# Revit family: P300300-031
name_source: partatom
category: Lighting Fixtures
revit_build: Autodesk Revit 2014 (Build: 20130308_1515(x64)
units: mm (PartAtom-declared; Revit-internal decimal feet)

## types (1)
- P300300-031
    Apparent Load = 100 VA
    Assembly Code = D5020200
    Connector Description = Lighting Connector
    Default Elevation = 48 "
    Description = Clarion Collection Two-Light Matte Black and Clear Glass Modern Style Bath Vanity Wall Light
    Features = Application: Embrace minimalist simplicity with the Clarion Collection 2-Light Matte Black Clear Glass Modern Bath Vanity Light ideal for any entryway, hallway, foyer, bedroom, sitting room, or bathroom.
Style: Perfect for contemporary, modern, and transitional style settings.
Finish: The square backplate and rounded light base are coated in a beautiful matte black finish for a modern aesthetic.
Materials: Constructed from steel to ensure a long product lifespan. Mount the light fixture vertically or horizontally.
Glass: Light sources glow from inside cylindrical shades for a crisp, clean look.
Bulbs: For ideal illumination, use 2 medium base T-lamp bulbs that are sold separately (60w max - LED/CFL/incandescent). Compatible with dimmable bulbs.
Dimensions: Measures 20-3/8-inch width by 5-inch height by 4-inch extends.
Certifications: cULus damp location listed.
Pairs With: Pairs with Equinox, Cahill, and Bonita collections.
Warranty: Our 1-Year Limited Warranty guarantees your complete satisfaction with your purchase and includes professional after-sales customer service support.
    Fixture distribution = Direct
    Glass = Paint - Hubbell - White Texture
    Gold = Hubbell - Gold
    Housing Material = Paint - Hubbell - Textured Camera Black
    Lamp = LED/CFL/incandescent
    Load Classification = Lighting
    Manufacturer = Progress Lighting
    Model = P300300-031
    Power Factor = 1
    Product Documentation Link = https://hubbellcdn.com
    Product Link = https://www.hubbell.com
    URL = https://www.hubbell.com
    Voltage = 120 V
    Warranty = 1 year Warranty
    Wattage Comments = 100W
    Watts = 100 W

## geometry (parser evidence)
native form markers: Sweep x5
no freeform markers — native parametric forms only
